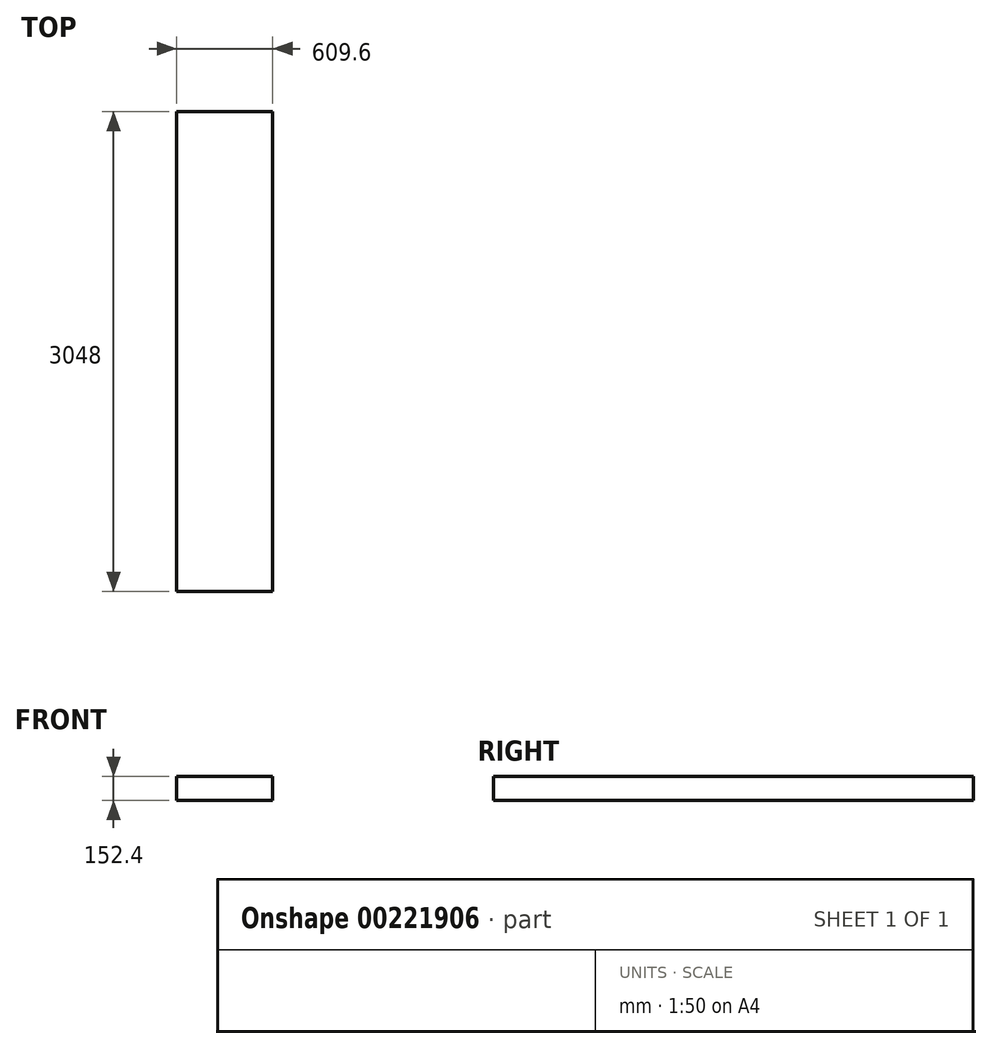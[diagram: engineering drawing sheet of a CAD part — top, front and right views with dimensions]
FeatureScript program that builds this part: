
annotation { "Feature Type Name" : "Feature", "Feature Type Description" : "" }
export const myFeature = defineFeature(function(context is Context, id is Id, definition is map)
    precondition{}
    {
        {
            var Q0;
            Q0=qCreatedBy(makeId("Front.planeOp"),FACE);
            var sketch = newSketch(context, id + "F0", { "sketchPlane" : qUnion([Q0])});
            skLineSegment(sketch, "E0.bottom", {"start": v(304.8, -76.2) * mm, "end": v(-304.8, -76.2) * mm});
            skLineSegment(sketch, "E0.top", {"start": v(304.8, 76.2) * mm, "end": v(-304.8, 76.2) * mm});
            skLineSegment(sketch, "E0.left", {"start": v(304.8, -76.2) * mm, "end": v(304.8, 76.2) * mm});
            skLineSegment(sketch, "E0.right", {"start": v(-304.8, -76.2) * mm, "end": v(-304.8, 76.2) * mm});
            skPoint(sketch, "E0.middle", {"position": v(0, 0) * mm});
            skSolve(sketch);
        }
        {
            var Q0;
            Q0 = qSketchRegion(id + "F0", true);
            extrude(context, id + "F1", {"entities" : qUnion([Q0]), "depth" : 3048 * mm});
        }
    });
